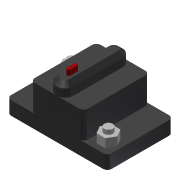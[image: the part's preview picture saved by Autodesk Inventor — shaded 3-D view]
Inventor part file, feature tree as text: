
AUTODESK INVENTOR PART (.ipt)
format: ipt  version: 2013 (Build 170138000, 138)  size: 184,832 bytes
history: native  units: in
note: dims shown in document units (in); Inventor stores cm internally (conversion verified against a paired STEP export)
features: extrude x6, sketch x6, fillet x2, projected_geometry x2, chamfer x1
ambient origin geometry x8: Origin, YZ Plane, XZ Plane, XY Plane, X Axis, Y Axis, Z Axis, Center Point
bodies: Solid1 (feature_tree), Solid2 (feature_tree), Solid3 (feature_tree)
feature tree (17):
  extrude  "Extrusion1"  Depth=1.9in
  extrude  "Extrusion2"  Depth=1.53in
  extrude  "Extrusion3"  Depth=0.5in
  fillet  "Fillet1"  Radius=0.35in
  chamfer  "Chamfer1"  Distance=0.125in Angle=45.0deg
  extrude  "Extrusion4"  Depth=0.1in
  extrude  "Extrusion5"  Depth=0.15in TaperAngle=0.0deg
  extrude  "Extrusion6"  Depth=0.4375in
  fillet  "Fillet2"  Radius=0.375in
  sketch  "Sketch2"  dims[d2=2.9in d3=1.9in]
  sketch  "Sketch3"  dims[d4=0.39in d5=0.0in d6=1.53in]
  sketch  "Sketch4"  dims[d7=0.769in d8=0.0in d9=0.5in d10=0.35in d11=0.0in]
  sketch  "Sketch5"  dims[d12=0.25in d13=0.125in d14=0.125in d15=45.0deg]
  sketch  "Sketch6"  dims[d16=0.2in d18=0.1in]
  projected_geometry  "Projected Loop1"
  sketch  "Sketch7"  dims[d19=0.1in d20=0.15in d21=0.0in d22=0.4375in d23=0.375in d24=0.375in d25=0.4375in d26=0.25in d27=0.0in d28=0.25in d29=0.25in d30=0.125in d31=0.0in d32=0.125in]
  projected_geometry  "Projected Loop2"
